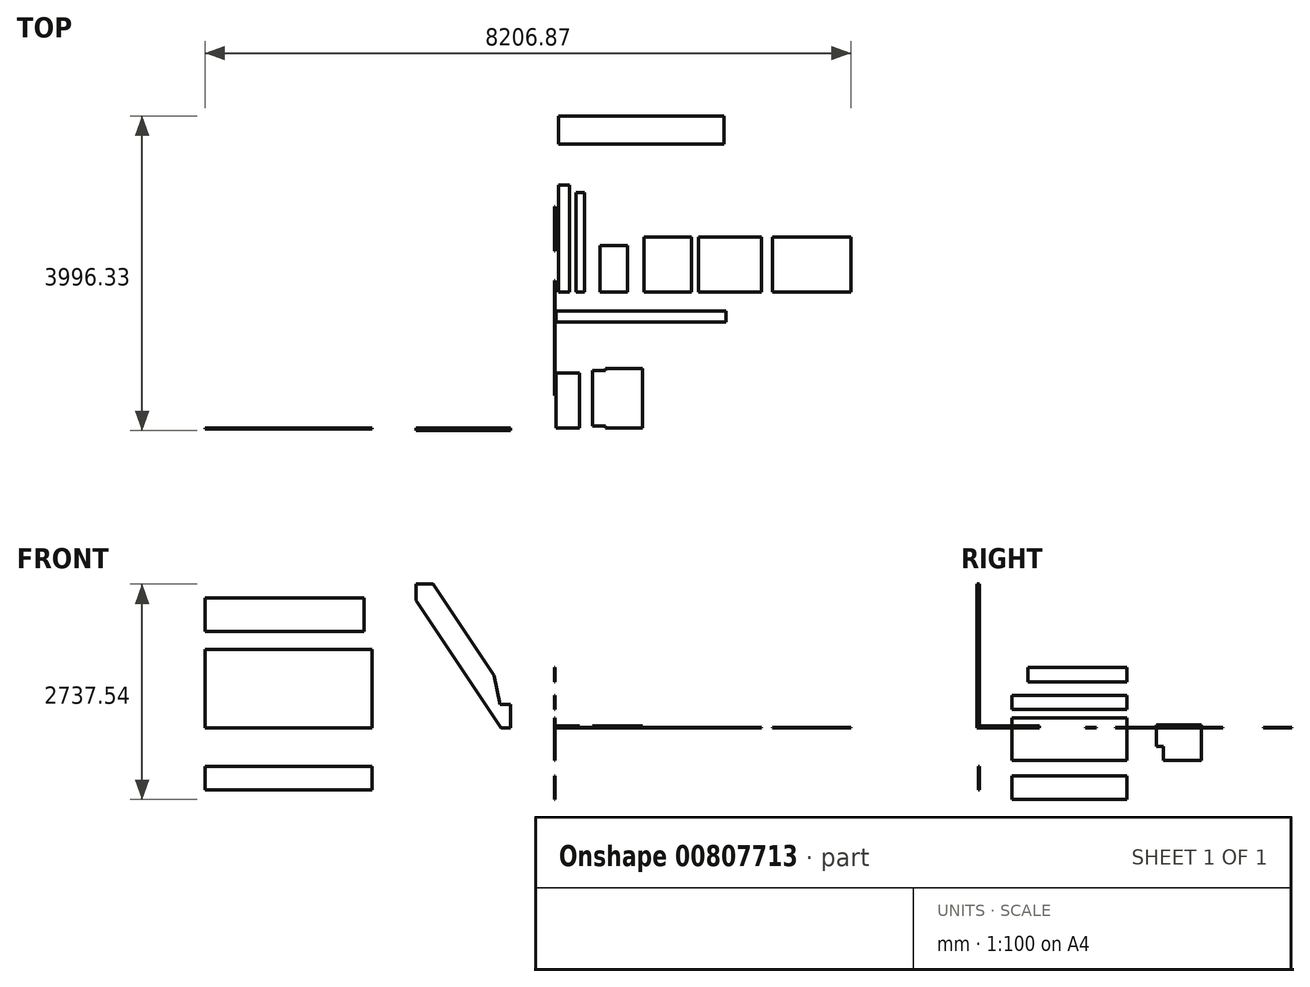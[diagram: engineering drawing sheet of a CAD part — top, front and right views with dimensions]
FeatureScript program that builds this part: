
annotation { "Feature Type Name" : "Feature", "Feature Type Description" : "" }
export const myFeature = defineFeature(function(context is Context, id is Id, definition is map)
    precondition{}
    {
        {
            var Q0;
            Q0=qCreatedBy(makeId("Top.planeOp"),FACE);
            var sketch = newSketch(context, id + "F0", { "sketchPlane" : qUnion([Q0])});
            skLineSegment(sketch, "E0.bottom", {"start": v(22.76, 700.45) * mm, "end": v(322.76, 700.45) * mm});
            skLineSegment(sketch, "E0.top", {"start": v(22.76, 0.45) * mm, "end": v(322.76, 0.45) * mm});
            skLineSegment(sketch, "E0.left", {"start": v(22.76, 700.45) * mm, "end": v(22.76, 0.45) * mm});
            skLineSegment(sketch, "E0.right", {"start": v(322.76, 700.45) * mm, "end": v(322.76, 0.45) * mm});
            skLineSegment(sketch, "E1.bottom", {"start": v(649.81, 760.45) * mm, "end": v(1117.45, 760.45) * mm});
            skLineSegment(sketch, "E1.top", {"start": v(649.81, 0.45) * mm, "end": v(1117.45, 0.45) * mm});
            skLineSegment(sketch, "E1.left", {"start": v(482.45, 730.45) * mm, "end": v(482.45, 30.45) * mm});
            skLineSegment(sketch, "E1.right", {"start": v(1117.45, 760.45) * mm, "end": v(1117.45, 0.45) * mm});
            skLineSegment(sketch, "E2", {"start": v(482.45, 30.45) * mm, "end": v(649.81, 30.45) * mm});
            skLineSegment(sketch, "E3", {"start": v(649.81, 30.45) * mm, "end": v(649.81, 0.45) * mm});
            skPoint(sketch, "E4", {"position": v(649.81, 730.45) * mm});
            skLineSegment(sketch, "E5.bottom", {"start": v(649.81, 730.45) * mm, "end": v(482.45, 730.45) * mm});
            skLineSegment(sketch, "E5.left", {"start": v(649.81, 730.45) * mm, "end": v(649.81, 760.45) * mm});
            skLineSegment(sketch, "E6.bottom", {"start": v(22.76, 1488.95) * mm, "end": v(2182.76, 1488.95) * mm});
            skLineSegment(sketch, "E6.top", {"start": v(22.76, 1348.95) * mm, "end": v(2182.76, 1348.95) * mm});
            skLineSegment(sketch, "E6.left", {"start": v(22.76, 1488.95) * mm, "end": v(22.76, 1348.95) * mm});
            skLineSegment(sketch, "E6.right", {"start": v(2182.76, 1488.95) * mm, "end": v(2182.76, 1348.95) * mm});
            skLineSegment(sketch, "E7.bottom", {"start": v(193.96, 1730.9) * mm, "end": v(53.96, 1730.9) * mm});
            skLineSegment(sketch, "E7.top", {"start": v(193.96, 3090.9) * mm, "end": v(53.96, 3090.9) * mm});
            skLineSegment(sketch, "E7.left", {"start": v(193.96, 1730.9) * mm, "end": v(193.96, 3090.9) * mm});
            skLineSegment(sketch, "E7.right", {"start": v(53.96, 1730.9) * mm, "end": v(53.96, 3090.9) * mm});
            skLineSegment(sketch, "E8.bottom", {"start": v(273.8, 1730.9) * mm, "end": v(383.8, 1730.9) * mm});
            skLineSegment(sketch, "E8.top", {"start": v(273.8, 2990.9) * mm, "end": v(383.8, 2990.9) * mm});
            skLineSegment(sketch, "E8.left", {"start": v(273.8, 1730.9) * mm, "end": v(273.8, 2990.9) * mm});
            skLineSegment(sketch, "E8.right", {"start": v(383.8, 1730.9) * mm, "end": v(383.8, 2990.9) * mm});
            skLineSegment(sketch, "E9.bottom", {"start": v(53.96, 3606.33) * mm, "end": v(2153.96, 3606.33) * mm});
            skLineSegment(sketch, "E9.top", {"start": v(53.96, 3966.33) * mm, "end": v(2153.96, 3966.33) * mm});
            skLineSegment(sketch, "E9.left", {"start": v(53.96, 3606.33) * mm, "end": v(53.96, 3966.33) * mm});
            skLineSegment(sketch, "E9.right", {"start": v(2153.96, 3606.33) * mm, "end": v(2153.96, 3966.33) * mm});
            skLineSegment(sketch, "E10.bottom", {"start": v(577.4, 1730.9) * mm, "end": v(927.4, 1730.9) * mm});
            skLineSegment(sketch, "E10.top", {"start": v(577.4, 2320.9) * mm, "end": v(927.4, 2320.9) * mm});
            skLineSegment(sketch, "E10.left", {"start": v(577.4, 1730.9) * mm, "end": v(577.4, 2320.9) * mm});
            skLineSegment(sketch, "E10.right", {"start": v(927.4, 1730.9) * mm, "end": v(927.4, 2320.9) * mm});
            skLineSegment(sketch, "E11.bottom", {"start": v(1142.14, 1730.9) * mm, "end": v(1742.14, 1730.9) * mm});
            skLineSegment(sketch, "E11.top", {"start": v(1142.14, 2430.9) * mm, "end": v(1742.14, 2430.9) * mm});
            skLineSegment(sketch, "E11.left", {"start": v(1142.14, 1730.9) * mm, "end": v(1142.14, 2430.9) * mm});
            skLineSegment(sketch, "E11.right", {"start": v(1742.14, 1730.9) * mm, "end": v(1742.14, 2430.9) * mm});
            skLineSegment(sketch, "E12.bottom", {"start": v(1832.3, 1730.9) * mm, "end": v(2632.3, 1730.9) * mm});
            skLineSegment(sketch, "E12.top", {"start": v(1832.3, 2430.9) * mm, "end": v(2632.3, 2430.9) * mm});
            skLineSegment(sketch, "E12.left", {"start": v(1832.3, 1730.9) * mm, "end": v(1832.3, 2430.9) * mm});
            skLineSegment(sketch, "E12.right", {"start": v(2632.3, 1730.9) * mm, "end": v(2632.3, 2430.9) * mm});
            skLineSegment(sketch, "E13.bottom", {"start": v(2769.63, 1730.9) * mm, "end": v(3769.63, 1730.9) * mm});
            skLineSegment(sketch, "E13.top", {"start": v(2769.63, 2430.9) * mm, "end": v(3769.63, 2430.9) * mm});
            skLineSegment(sketch, "E13.left", {"start": v(2769.63, 1730.9) * mm, "end": v(2769.63, 2430.9) * mm});
            skLineSegment(sketch, "E13.right", {"start": v(3769.63, 1730.9) * mm, "end": v(3769.63, 2430.9) * mm});
            skSolve(sketch);
        }
        {
            var Q0;
            Q0=makeQuery(id+"F0.imprint","IMPRINT",FACE,{"disambiguationData":[TD([[makeQuery(id+"F0.imprint","IMPRINT",EDGE,{"derivedFrom":sQuery(id+"F0.wireOp",EDGE,"E0.bottom")}),-1.0]])]});
            var Q1;
            Q1=makeQuery(id+"F0.imprint","IMPRINT",FACE,{"disambiguationData":[TD([[makeQuery(id+"F0.imprint","IMPRINT",EDGE,{"derivedFrom":sQuery(id+"F0.wireOp",EDGE,"E1.bottom")}),-1.0]])]});
            extrude(context, id + "F1", {"entities" : qUnion([Q0, Q1]), "depth" : 30 * mm, "offsetDistance" : 25 * mm});
        }
        {
            var Q0;
            Q0=makeQuery(id+"F0.imprint","IMPRINT",FACE,{"disambiguationData":[TD([[makeQuery(id+"F0.imprint","IMPRINT",EDGE,{"derivedFrom":sQuery(id+"F0.wireOp",EDGE,"E6.bottom")}),-1.0]])]});
            var Q1;
            Q1=makeQuery(id+"F0.imprint","IMPRINT",FACE,{"disambiguationData":[TD([[makeQuery(id+"F0.imprint","IMPRINT",EDGE,{"derivedFrom":sQuery(id+"F0.wireOp",EDGE,"E7.bottom")}),-1.0]])]});
            var Q2;
            Q2=makeQuery(id+"F0.imprint","IMPRINT",FACE,{"disambiguationData":[TD([[makeQuery(id+"F0.imprint","IMPRINT",EDGE,{"derivedFrom":sQuery(id+"F0.wireOp",EDGE,"E8.bottom")}),1.0]])]});
            var Q3;
            Q3=makeQuery(id+"F0.imprint","IMPRINT",FACE,{"disambiguationData":[TD([[makeQuery(id+"F0.imprint","IMPRINT",EDGE,{"derivedFrom":sQuery(id+"F0.wireOp",EDGE,"E9.bottom")}),1.0]])]});
            var Q4;
            Q4=makeQuery(id+"F0.imprint","IMPRINT",FACE,{"disambiguationData":[TD([[makeQuery(id+"F0.imprint","IMPRINT",EDGE,{"derivedFrom":sQuery(id+"F0.wireOp",EDGE,"E10.bottom")}),1.0]])]});
            var Q5;
            Q5=makeQuery(id+"F0.imprint","IMPRINT",FACE,{"disambiguationData":[TD([[makeQuery(id+"F0.imprint","IMPRINT",EDGE,{"derivedFrom":sQuery(id+"F0.wireOp",EDGE,"E11.bottom")}),1.0]])]});
            var Q6;
            Q6=makeQuery(id+"F0.imprint","IMPRINT",FACE,{"disambiguationData":[TD([[makeQuery(id+"F0.imprint","IMPRINT",EDGE,{"derivedFrom":sQuery(id+"F0.wireOp",EDGE,"E12.bottom")}),1.0]])]});
            var Q7;
            Q7=makeQuery(id+"F0.imprint","IMPRINT",FACE,{"disambiguationData":[TD([[makeQuery(id+"F0.imprint","IMPRINT",EDGE,{"derivedFrom":sQuery(id+"F0.wireOp",EDGE,"E13.bottom")}),1.0]])]});
            extrude(context, id + "F2", {"entities" : qUnion([Q0, Q1, Q2, Q3, Q4, Q5, Q6, Q7]), "depth" : 10 * mm, "offsetDistance" : 25 * mm});
        }
        {
            var Q0;
            Q0=qCreatedBy(makeId("Front.planeOp"),FACE);
            var sketch = newSketch(context, id + "F3", { "sketchPlane" : qUnion([Q0])});
            skLineSegment(sketch, "E14.bottom", {"start": v(-557.23, 0) * mm, "end": v(-677.74, 0) * mm});
            skLineSegment(sketch, "E14.right", {"start": v(-1757.23, 1619.24) * mm, "end": v(-1757.23, 1830) * mm});
            skLineSegment(sketch, "E15", {"start": v(-1537.18, 1830) * mm, "end": v(-763.4, 669.33) * mm});
            skLineSegment(sketch, "E16", {"start": v(-1757.23, 1619.24) * mm, "end": v(-677.74, 0) * mm});
            skLineSegment(sketch, "E17", {"start": v(-557.23, 300) * mm, "end": v(-557.23, 0) * mm});
            skLineSegment(sketch, "E18", {"start": v(-689.86, 300) * mm, "end": v(-763.4, 669.33) * mm});
            skLineSegment(sketch, "E19.bottom", {"start": v(-2317.24, 0) * mm, "end": v(-4437.24, 0) * mm});
            skLineSegment(sketch, "E19.top", {"start": v(-2317.24, 1000) * mm, "end": v(-4437.24, 1000) * mm});
            skLineSegment(sketch, "E19.left", {"start": v(-2317.24, 0) * mm, "end": v(-2317.24, 1000) * mm});
            skLineSegment(sketch, "E19.right", {"start": v(-4437.24, 0) * mm, "end": v(-4437.24, 1000) * mm});
            skLineSegment(sketch, "E20", {"start": v(-1537.18, 1830) * mm, "end": v(-1757.23, 1830) * mm});
            skLineSegment(sketch, "E21", {"start": v(-689.86, 300) * mm, "end": v(-557.23, 300) * mm});
            skLineSegment(sketch, "E22.bottom", {"start": v(-4437.24, 1224.89) * mm, "end": v(-2417.24, 1224.89) * mm});
            skLineSegment(sketch, "E22.top", {"start": v(-4437.24, 1654.89) * mm, "end": v(-2417.24, 1654.89) * mm});
            skLineSegment(sketch, "E22.left", {"start": v(-4437.24, 1224.89) * mm, "end": v(-4437.24, 1654.89) * mm});
            skLineSegment(sketch, "E22.right", {"start": v(-2417.24, 1224.89) * mm, "end": v(-2417.24, 1654.89) * mm});
            skLineSegment(sketch, "E23.bottom", {"start": v(-4437.24, -487.35) * mm, "end": v(-2317.24, -487.35) * mm});
            skLineSegment(sketch, "E23.top", {"start": v(-4437.24, -787.35) * mm, "end": v(-2317.24, -787.35) * mm});
            skLineSegment(sketch, "E23.left", {"start": v(-4437.24, -487.35) * mm, "end": v(-4437.24, -787.35) * mm});
            skLineSegment(sketch, "E23.right", {"start": v(-2317.24, -487.35) * mm, "end": v(-2317.24, -787.35) * mm});
            skSolve(sketch);
        }
        {
            var Q0;
            Q0=makeQuery(id+"F3.imprint","IMPRINT",FACE,{"disambiguationData":[TD([[makeQuery(id+"F3.imprint","IMPRINT",EDGE,{"derivedFrom":sQuery(id+"F3.wireOp",EDGE,"E14.bottom")}),-1.0]])]});
            extrude(context, id + "F4", {"entities" : qUnion([Q0]), "depth" : 30 * mm, "offsetDistance" : 25 * mm});
        }
        {
            var Q0;
            Q0=makeQuery(id+"F3.imprint","IMPRINT",FACE,{"disambiguationData":[TD([[makeQuery(id+"F3.imprint","IMPRINT",EDGE,{"derivedFrom":sQuery(id+"F3.wireOp",EDGE,"E19.bottom")}),-1.0]])]});
            var Q1;
            Q1=makeQuery(id+"F3.imprint","IMPRINT",FACE,{"disambiguationData":[TD([[makeQuery(id+"F3.imprint","IMPRINT",EDGE,{"derivedFrom":sQuery(id+"F3.wireOp",EDGE,"E22.bottom")}),1.0]])]});
            var Q2;
            Q2=makeQuery(id+"F3.imprint","IMPRINT",FACE,{"disambiguationData":[TD([[makeQuery(id+"F3.imprint","IMPRINT",EDGE,{"derivedFrom":sQuery(id+"F3.wireOp",EDGE,"E23.bottom")}),-1.0]])]});
            extrude(context, id + "F5", {"entities" : qUnion([Q0, Q1, Q2]), "depth" : 10 * mm, "offsetDistance" : 25 * mm});
        }
        {
            var Q0;
            Q0=qCreatedBy(makeId("Right.planeOp"),FACE);
            var sketch = newSketch(context, id + "F6", { "sketchPlane" : qUnion([Q0])});
            skLineSegment(sketch, "E24.bottom", {"start": v(414.29, 237.08) * mm, "end": v(1874.29, 237.08) * mm});
            skLineSegment(sketch, "E24.top", {"start": v(414.29, 417.08) * mm, "end": v(1874.29, 417.08) * mm});
            skLineSegment(sketch, "E24.left", {"start": v(414.29, 237.08) * mm, "end": v(414.29, 417.08) * mm});
            skLineSegment(sketch, "E24.right", {"start": v(1874.29, 237.08) * mm, "end": v(1874.29, 417.08) * mm});
            skLineSegment(sketch, "E25.bottom", {"start": v(414.29, 128.08) * mm, "end": v(1874.29, 128.08) * mm});
            skLineSegment(sketch, "E25.top", {"start": v(414.29, -411.92) * mm, "end": v(1874.29, -411.92) * mm});
            skLineSegment(sketch, "E25.left", {"start": v(414.29, 128.08) * mm, "end": v(414.29, -411.92) * mm});
            skLineSegment(sketch, "E25.right", {"start": v(1874.29, 128.08) * mm, "end": v(1874.29, -411.92) * mm});
            skLineSegment(sketch, "E26.bottom", {"start": v(2338.66, -411.92) * mm, "end": v(2818.66, -411.92) * mm});
            skLineSegment(sketch, "E26.top", {"start": v(2248.66, 38.08) * mm, "end": v(2818.66, 38.08) * mm});
            skLineSegment(sketch, "E26.right", {"start": v(2818.66, -411.92) * mm, "end": v(2818.66, 38.08) * mm});
            skLineSegment(sketch, "E27", {"start": v(2248.66, 38.08) * mm, "end": v(2248.66, -231.92) * mm});
            skLineSegment(sketch, "E28", {"start": v(2248.66, -231.92) * mm, "end": v(2338.66, -231.92) * mm});
            skLineSegment(sketch, "E29", {"start": v(2338.66, -231.92) * mm, "end": v(2338.66, -411.92) * mm});
            skLineSegment(sketch, "E30.bottom", {"start": v(1874.29, 589.15) * mm, "end": v(614.29, 589.15) * mm});
            skLineSegment(sketch, "E30.top", {"start": v(1874.29, 769.15) * mm, "end": v(614.29, 769.15) * mm});
            skLineSegment(sketch, "E30.left", {"start": v(1874.29, 589.15) * mm, "end": v(1874.29, 769.15) * mm});
            skLineSegment(sketch, "E30.right", {"start": v(614.29, 589.15) * mm, "end": v(614.29, 769.15) * mm});
            skLineSegment(sketch, "E31.bottom", {"start": v(1874.29, -607.54) * mm, "end": v(414.29, -607.54) * mm});
            skLineSegment(sketch, "E31.top", {"start": v(1874.29, -907.54) * mm, "end": v(414.29, -907.54) * mm});
            skLineSegment(sketch, "E31.left", {"start": v(1874.29, -607.54) * mm, "end": v(1874.29, -907.54) * mm});
            skLineSegment(sketch, "E31.right", {"start": v(414.29, -607.54) * mm, "end": v(414.29, -907.54) * mm});
            skSolve(sketch);
        }
        {
            var Q0;
            Q0=makeQuery(id+"F6.imprint","IMPRINT",FACE,{"disambiguationData":[TD([[makeQuery(id+"F6.imprint","IMPRINT",EDGE,{"derivedFrom":sQuery(id+"F6.wireOp",EDGE,"E24.bottom")}),1.0]])]});
            var Q1;
            Q1=makeQuery(id+"F6.imprint","IMPRINT",FACE,{"disambiguationData":[TD([[makeQuery(id+"F6.imprint","IMPRINT",EDGE,{"derivedFrom":sQuery(id+"F6.wireOp",EDGE,"E25.bottom")}),-1.0]])]});
            var Q2;
            Q2=makeQuery(id+"F6.imprint","IMPRINT",FACE,{"disambiguationData":[TD([[makeQuery(id+"F6.imprint","IMPRINT",EDGE,{"derivedFrom":sQuery(id+"F6.wireOp",EDGE,"E26.bottom")}),1.0]])]});
            var Q3;
            Q3=makeQuery(id+"F6.imprint","IMPRINT",FACE,{"disambiguationData":[TD([[makeQuery(id+"F6.imprint","IMPRINT",EDGE,{"derivedFrom":sQuery(id+"F6.wireOp",EDGE,"E30.bottom")}),-1.0]])]});
            var Q4;
            Q4=makeQuery(id+"F6.imprint","IMPRINT",FACE,{"disambiguationData":[TD([[makeQuery(id+"F6.imprint","IMPRINT",EDGE,{"derivedFrom":sQuery(id+"F6.wireOp",EDGE,"E31.bottom")}),1.0]])]});
            extrude(context, id + "F7", {"entities" : qUnion([Q0, Q1, Q2, Q3, Q4]), "depth" : 10 * mm, "offsetDistance" : 25 * mm});
        }
    });
